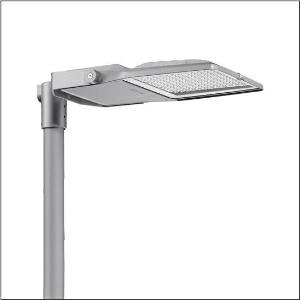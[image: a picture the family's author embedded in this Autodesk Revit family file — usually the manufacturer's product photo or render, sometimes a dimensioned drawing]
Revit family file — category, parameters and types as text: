
# Revit family: floodlight_fl_21_iq_midi___pl52_5xa7781e2d3a_77a1
name_source: partatom
category: Lighting Fixtures
units: mm (PartAtom-declared; Revit-internal decimal feet)

## family parameters
Cut with Voids When Loaded = No
Host = Face
Light Source = No
Part Type = Normal
Room Calculation Point = No
Round Connector Dimension = Use Diameter
Shared = No

## types (1)
- --- (1 x LED, 26850 lm, 208.1 W, 3000K)
    Apparent Load = 208 VA
    CIE Flux Codes = 26 60 98 100 100
    Color Rendering = 70
    Color Temperature = 3000K
    Default Elevation = 1800 mm
    Description = Floodlight FL 21 iQ midi, floodlight, primary light control with lens, of PMMA, primary optical cover: protective disc, of toughened safety glass, transparent, light distribution: PL52, light emission: direct distribution, installation type: surface-mounted, LED, High Power LED, rated luminous flux: 26.850lm, luminous efficacy: 129lm/W, light colour: 730, colour temperature: 3000K, control gear: ECG iQ, control: optimised constant luminous flux control (CLO 2.0), Desk-Remote (wireless, voltage-free reading and setting of iQ features in the workshop via application-optimized NFC function/RFID function), Light-Fading, Smart-Wire, Night-Set, Lumen-Switch, Temp-Guard, Auto-Match, with terminal, 6-pole, mains connection: 220..240V, AC, 50/60Hz, start of lifetime: 208W, end of service life: 227W, reduction: 90W, luminaire housing, of diecast aluminium, powder-coated, Siteco® metallic grey (DB 702S), corrosivity category C5 mid according to DIN EN ISO 12944, sealing non-destructively replaceable, please order mast flange separately, mast bracket, of steel, galvanised, powder-coated, Siteco® metallic grey (DB 702S), protection rating (complete): IP66, insulation class (complete): insulation class II (safety insulation), certification: CE, ENEC, VDE, protection symbol: D, impact resistance: IK08, permissible operating ambient temperature: -40..+40°C, permissible operating ambient temperature for outdoor applications: -40..+50°C, standard: DIN EN 12944, LABS conformity tested according to VDMA 24364:2018-05, packaging unit: 1 piece

Light Distribution: PL52
    Height = 76 mm
    Lamp = 1 x LED
    Lamp Light Flux = 26850 lm
    Lamp Power = 208.1 W
    Lamp count = 1
    Length = 657 mm
    Luminous efficacy = 129 lm/W
    Manufacturer = Siteco
    ModVariant = No
    Model = 5XA7781E2D3A
    Number of Poles = 1
    OnlyDefault = Yes
    Power Factor = 1
    Product Name = Floodlight FL 21 iQ midi | PL52
    Product group = floodlight | pylon annexe
    ProductGroupID = 6200
    Protection Class = Protection class II
    Protection Degree = IP 66
    RLX_Detail_Level = 1
    RLX_Emergency_Light_Flux = 0 lm
    RLX_Emergency_Type = 0
    RLX_Emergency_Type_DB = No
    RlxData = <blob elided: 154029 chars, md5=c0f2f961>
    Socket = socket
    Standby Power = 0 W
    System Light Flux = 26850 lm
    System Power = 208 W
    Type Comments = factory setting: luminous flux: 100 % | dim-lin: 254 | 710 mA
    Type Image = l_1007123.jpg
    URL = http://relux.com
    VarID = @adj_075123
    Voltage = 0 V
    Weight = 0.00 kg
    Width = 442 mm

## geometry (parser evidence)
native form markers: Blend x4, Sweep x15
no freeform markers — native parametric forms only
